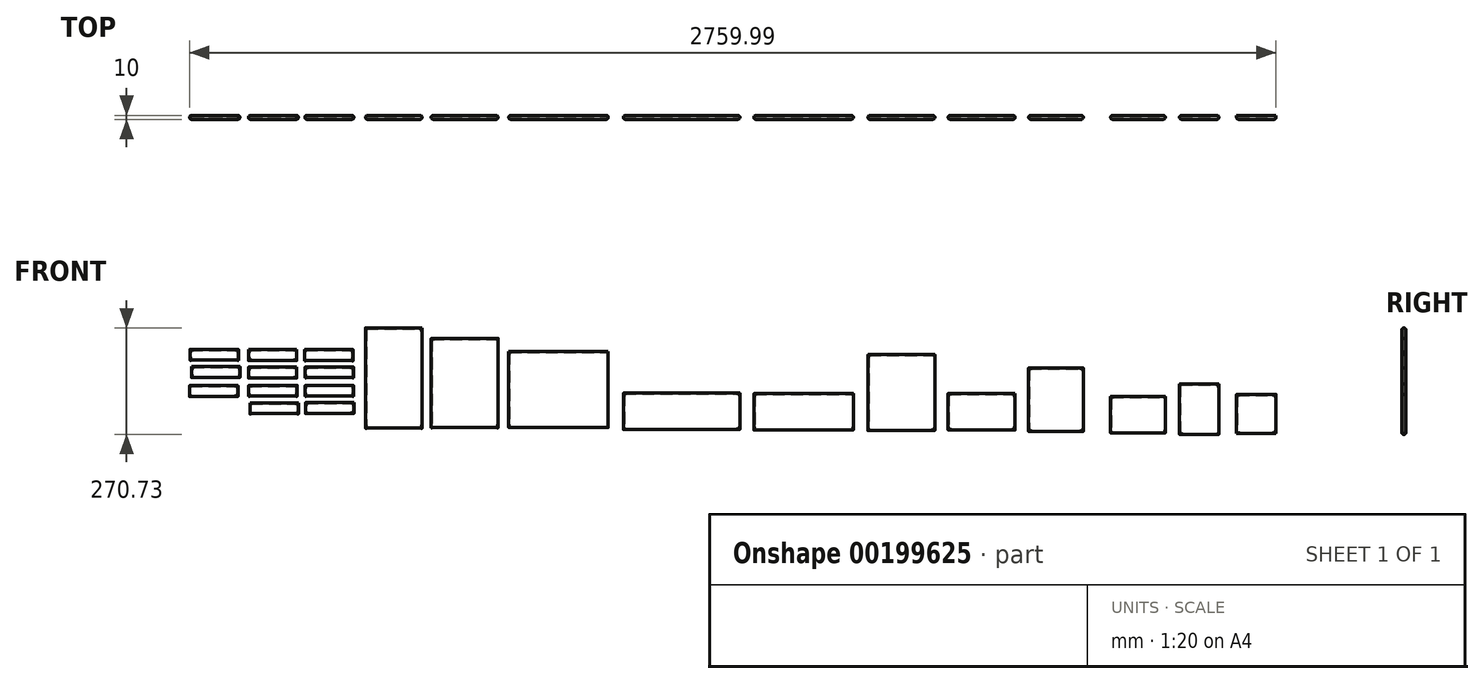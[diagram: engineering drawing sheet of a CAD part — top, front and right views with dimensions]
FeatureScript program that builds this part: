
annotation { "Feature Type Name" : "Feature", "Feature Type Description" : "" }
export const myFeature = defineFeature(function(context is Context, id is Id, definition is map)
    precondition{}
    {
        {
            var Q0;
            Q0=qCreatedBy(makeId("Front.planeOp"),FACE);
            var sketch = newSketch(context, id + "F0", { "sketchPlane" : qUnion([Q0])});
            skLineSegment(sketch, "E0.bottom", {"start": v(-185.42, 51.02) * mm, "end": v(-62.42, 51.02) * mm});
            skLineSegment(sketch, "E0.top", {"start": v(-185.42, 79.02) * mm, "end": v(-62.42, 79.02) * mm});
            skLineSegment(sketch, "E0.left", {"start": v(-185.42, 51.02) * mm, "end": v(-185.42, 79.02) * mm});
            skLineSegment(sketch, "E0.right", {"start": v(-62.42, 51.02) * mm, "end": v(-62.42, 79.02) * mm});
            skLineSegment(sketch, "E1.bottom", {"start": v(-184.61, -39.22) * mm, "end": v(-61.61, -39.22) * mm});
            skLineSegment(sketch, "E1.top", {"start": v(-184.61, -11.22) * mm, "end": v(-61.61, -11.22) * mm});
            skLineSegment(sketch, "E1.left", {"start": v(-184.61, -39.22) * mm, "end": v(-184.61, -11.22) * mm});
            skLineSegment(sketch, "E1.right", {"start": v(-61.61, -39.22) * mm, "end": v(-61.61, -11.22) * mm});
            skLineSegment(sketch, "E2.bottom", {"start": v(-183.78, -83.5) * mm, "end": v(-60.78, -83.5) * mm});
            skLineSegment(sketch, "E2.top", {"start": v(-183.78, -55.5) * mm, "end": v(-60.78, -55.5) * mm});
            skLineSegment(sketch, "E2.left", {"start": v(-183.78, -83.5) * mm, "end": v(-183.78, -55.5) * mm});
            skLineSegment(sketch, "E2.right", {"start": v(-60.78, -83.5) * mm, "end": v(-60.78, -55.5) * mm});
            skLineSegment(sketch, "E3.bottom", {"start": v(-328.72, 51.62) * mm, "end": v(-205.72, 51.62) * mm});
            skLineSegment(sketch, "E3.top", {"start": v(-328.72, 79.62) * mm, "end": v(-205.72, 79.62) * mm});
            skLineSegment(sketch, "E3.left", {"start": v(-328.72, 51.62) * mm, "end": v(-328.72, 79.62) * mm});
            skLineSegment(sketch, "E3.right", {"start": v(-205.72, 51.62) * mm, "end": v(-205.72, 79.62) * mm});
            skLineSegment(sketch, "E4.bottom", {"start": v(-184.79, 7.45) * mm, "end": v(-61.79, 7.45) * mm});
            skLineSegment(sketch, "E4.top", {"start": v(-184.79, 35.45) * mm, "end": v(-61.79, 35.45) * mm});
            skLineSegment(sketch, "E4.left", {"start": v(-184.79, 7.45) * mm, "end": v(-184.79, 35.45) * mm});
            skLineSegment(sketch, "E4.right", {"start": v(-61.79, 7.45) * mm, "end": v(-61.79, 35.45) * mm});
            skLineSegment(sketch, "E5.bottom", {"start": v(-328.7, 6.95) * mm, "end": v(-205.7, 6.95) * mm});
            skLineSegment(sketch, "E5.top", {"start": v(-328.7, 34.95) * mm, "end": v(-205.7, 34.95) * mm});
            skLineSegment(sketch, "E5.left", {"start": v(-328.7, 6.95) * mm, "end": v(-328.7, 34.95) * mm});
            skLineSegment(sketch, "E5.right", {"start": v(-205.7, 6.95) * mm, "end": v(-205.7, 34.95) * mm});
            skLineSegment(sketch, "E6.bottom", {"start": v(-477.03, 51.95) * mm, "end": v(-354.03, 51.95) * mm});
            skLineSegment(sketch, "E6.top", {"start": v(-477.03, 79.95) * mm, "end": v(-354.03, 79.95) * mm});
            skLineSegment(sketch, "E6.left", {"start": v(-477.03, 51.95) * mm, "end": v(-477.03, 79.95) * mm});
            skLineSegment(sketch, "E6.right", {"start": v(-354.03, 51.95) * mm, "end": v(-354.03, 79.95) * mm});
            skLineSegment(sketch, "E7.bottom", {"start": v(-473.24, 7.86) * mm, "end": v(-350.24, 7.86) * mm});
            skLineSegment(sketch, "E7.top", {"start": v(-473.24, 35.86) * mm, "end": v(-350.24, 35.86) * mm});
            skLineSegment(sketch, "E7.left", {"start": v(-473.24, 7.86) * mm, "end": v(-473.24, 35.86) * mm});
            skLineSegment(sketch, "E7.right", {"start": v(-350.24, 7.86) * mm, "end": v(-350.24, 35.86) * mm});
            skLineSegment(sketch, "E8.bottom", {"start": v(-478.2, -39.92) * mm, "end": v(-355.2, -39.92) * mm});
            skLineSegment(sketch, "E8.top", {"start": v(-478.2, -11.92) * mm, "end": v(-355.2, -11.92) * mm});
            skLineSegment(sketch, "E8.left", {"start": v(-478.2, -39.92) * mm, "end": v(-478.2, -11.92) * mm});
            skLineSegment(sketch, "E8.right", {"start": v(-355.2, -39.92) * mm, "end": v(-355.2, -11.92) * mm});
            skLineSegment(sketch, "E9.bottom", {"start": v(-324.63, -84.24) * mm, "end": v(-201.63, -84.24) * mm});
            skLineSegment(sketch, "E9.top", {"start": v(-324.63, -56.24) * mm, "end": v(-201.63, -56.24) * mm});
            skLineSegment(sketch, "E9.left", {"start": v(-324.63, -84.24) * mm, "end": v(-324.63, -56.24) * mm});
            skLineSegment(sketch, "E9.right", {"start": v(-201.63, -84.24) * mm, "end": v(-201.63, -56.24) * mm});
            skLineSegment(sketch, "E10.bottom", {"start": v(-327.71, -39.33) * mm, "end": v(-204.71, -39.33) * mm});
            skLineSegment(sketch, "E10.top", {"start": v(-327.71, -11.33) * mm, "end": v(-204.71, -11.33) * mm});
            skLineSegment(sketch, "E10.left", {"start": v(-327.71, -39.33) * mm, "end": v(-327.71, -11.33) * mm});
            skLineSegment(sketch, "E10.right", {"start": v(-204.71, -39.33) * mm, "end": v(-204.71, -11.33) * mm});
            skSolve(sketch);
        }
        {
            var Q0;
            Q0=qSketchRegion(id+"F0",true);
            extrude(context, id + "F1", {"entities" : qUnion([Q0]), "depth" : 10 * mm});
        }
        {
            var Q0;
            Q0=makeQuery(id+"F1.opExtrude","SWEPT_FACE",FACE,{"disambiguationData":[OSD([sQuery(id+"F0.wireOp",EDGE,"E0.bottom")])]});
            var Q1;
            Q1=makeQuery(id+"F1.opExtrude","SWEPT_FACE",FACE,{"disambiguationData":[OSD([sQuery(id+"F0.wireOp",EDGE,"E4.bottom")])]});
            var Q2;
            Q2=makeQuery(id+"F1.opExtrude","SWEPT_FACE",FACE,{"disambiguationData":[OSD([sQuery(id+"F0.wireOp",EDGE,"E7.bottom")])]});
            var Q3;
            Q3=makeQuery(id+"F1.opExtrude","SWEPT_FACE",FACE,{"disambiguationData":[OSD([sQuery(id+"F0.wireOp",EDGE,"E3.bottom")])]});
            var Q4;
            Q4=makeQuery(id+"F1.opExtrude","SWEPT_FACE",FACE,{"disambiguationData":[OSD([sQuery(id+"F0.wireOp",EDGE,"E6.bottom")])]});
            var Q5;
            Q5=makeQuery(id+"F1.opExtrude","SWEPT_FACE",FACE,{"disambiguationData":[OSD([sQuery(id+"F0.wireOp",EDGE,"E8.bottom")])]});
            var Q6;
            Q6=makeQuery(id+"F1.opExtrude","SWEPT_FACE",FACE,{"disambiguationData":[OSD([sQuery(id+"F0.wireOp",EDGE,"E9.bottom")])]});
            var Q7;
            Q7=makeQuery(id+"F1.opExtrude","SWEPT_FACE",FACE,{"disambiguationData":[OSD([sQuery(id+"F0.wireOp",EDGE,"E10.bottom")])]});
            var Q8;
            Q8=makeQuery(id+"F1.opExtrude","SWEPT_FACE",FACE,{"disambiguationData":[OSD([sQuery(id+"F0.wireOp",EDGE,"E5.bottom")])]});
            var Q9;
            Q9=makeQuery(id+"F1.opExtrude","SWEPT_FACE",FACE,{"disambiguationData":[OSD([sQuery(id+"F0.wireOp",EDGE,"E2.bottom")])]});
            var Q10;
            Q10=makeQuery(id+"F1.opExtrude","SWEPT_FACE",FACE,{"disambiguationData":[OSD([sQuery(id+"F0.wireOp",EDGE,"E1.bottom")])]});
            shell(context, id + "F2", {"entities" : qUnion([Q0, Q1, Q2, Q3, Q4, Q5, Q6, Q7, Q8, Q9, Q10]), "thickness" : 2.5 * mm});
        }
        {
            var Q0;
            Q0=qCreatedBy(makeId("Front.planeOp"),FACE);
            var sketch = newSketch(context, id + "F3", { "sketchPlane" : qUnion([Q0])});
            skLineSegment(sketch, "E11.bottom", {"start": v(-31.23, 134.3) * mm, "end": v(112.77, 134.3) * mm});
            skLineSegment(sketch, "E11.top", {"start": v(-31.23, -120.7) * mm, "end": v(112.77, -120.7) * mm});
            skLineSegment(sketch, "E11.left", {"start": v(-31.23, 134.3) * mm, "end": v(-31.23, -120.7) * mm});
            skLineSegment(sketch, "E11.right", {"start": v(112.77, 134.3) * mm, "end": v(112.77, -120.7) * mm});
            skLineSegment(sketch, "E12.bottom", {"start": v(135.53, 107.6) * mm, "end": v(305.53, 107.6) * mm});
            skLineSegment(sketch, "E12.top", {"start": v(135.53, -119.4) * mm, "end": v(305.53, -119.4) * mm});
            skLineSegment(sketch, "E12.left", {"start": v(135.53, 107.6) * mm, "end": v(135.53, -119.4) * mm});
            skLineSegment(sketch, "E12.right", {"start": v(305.53, 107.6) * mm, "end": v(305.53, -119.4) * mm});
            skLineSegment(sketch, "E13.bottom", {"start": v(332.44, 73.9) * mm, "end": v(585.44, 73.9) * mm});
            skLineSegment(sketch, "E13.top", {"start": v(332.44, -119.1) * mm, "end": v(585.44, -119.1) * mm});
            skLineSegment(sketch, "E13.left", {"start": v(332.44, 73.9) * mm, "end": v(332.44, -119.1) * mm});
            skLineSegment(sketch, "E13.right", {"start": v(585.44, 73.9) * mm, "end": v(585.44, -119.1) * mm});
            skLineSegment(sketch, "E14.bottom", {"start": v(623.81, -30.97) * mm, "end": v(919.81, -30.97) * mm});
            skLineSegment(sketch, "E14.top", {"start": v(623.81, -123.97) * mm, "end": v(919.81, -123.97) * mm});
            skLineSegment(sketch, "E14.left", {"start": v(623.81, -30.97) * mm, "end": v(623.81, -123.97) * mm});
            skLineSegment(sketch, "E14.right", {"start": v(919.81, -30.97) * mm, "end": v(919.81, -123.97) * mm});
            skLineSegment(sketch, "E15.bottom", {"start": v(955.2, -32.5) * mm, "end": v(1208.2, -32.5) * mm});
            skLineSegment(sketch, "E15.top", {"start": v(955.2, -125.5) * mm, "end": v(1208.2, -125.5) * mm});
            skLineSegment(sketch, "E15.left", {"start": v(955.2, -32.5) * mm, "end": v(955.2, -125.5) * mm});
            skLineSegment(sketch, "E15.right", {"start": v(1208.2, -32.5) * mm, "end": v(1208.2, -125.5) * mm});
            skLineSegment(sketch, "E16.bottom", {"start": v(1245.22, 66.68) * mm, "end": v(1415.22, 66.68) * mm});
            skLineSegment(sketch, "E16.top", {"start": v(1245.22, -126.32) * mm, "end": v(1415.22, -126.32) * mm});
            skLineSegment(sketch, "E16.left", {"start": v(1245.22, 66.68) * mm, "end": v(1245.22, -126.32) * mm});
            skLineSegment(sketch, "E16.right", {"start": v(1415.22, 66.68) * mm, "end": v(1415.22, -126.32) * mm});
            skLineSegment(sketch, "E17.bottom", {"start": v(1448.93, -32.02) * mm, "end": v(1618.93, -32.02) * mm});
            skLineSegment(sketch, "E17.top", {"start": v(1448.93, -125.02) * mm, "end": v(1618.93, -125.02) * mm});
            skLineSegment(sketch, "E17.left", {"start": v(1448.93, -32.02) * mm, "end": v(1448.93, -125.02) * mm});
            skLineSegment(sketch, "E17.right", {"start": v(1618.93, -32.02) * mm, "end": v(1618.93, -125.02) * mm});
            skLineSegment(sketch, "E18.bottom", {"start": v(1653.54, 32.98) * mm, "end": v(1792.54, 32.98) * mm});
            skLineSegment(sketch, "E18.top", {"start": v(1653.54, -129.02) * mm, "end": v(1792.54, -129.02) * mm});
            skLineSegment(sketch, "E18.left", {"start": v(1653.54, 32.98) * mm, "end": v(1653.54, -129.02) * mm});
            skLineSegment(sketch, "E18.right", {"start": v(1792.54, 32.98) * mm, "end": v(1792.54, -129.02) * mm});
            skLineSegment(sketch, "E19.bottom", {"start": v(1861.67, -40.12) * mm, "end": v(2000.67, -40.12) * mm});
            skLineSegment(sketch, "E19.top", {"start": v(1861.67, -133.12) * mm, "end": v(2000.67, -133.12) * mm});
            skLineSegment(sketch, "E19.left", {"start": v(1861.67, -40.12) * mm, "end": v(1861.67, -133.12) * mm});
            skLineSegment(sketch, "E19.right", {"start": v(2000.67, -40.12) * mm, "end": v(2000.67, -133.12) * mm});
            skLineSegment(sketch, "E20.bottom", {"start": v(2036.78, -8.43) * mm, "end": v(2136.78, -8.43) * mm});
            skLineSegment(sketch, "E20.top", {"start": v(2036.78, -136.43) * mm, "end": v(2136.78, -136.43) * mm});
            skLineSegment(sketch, "E20.left", {"start": v(2036.78, -8.43) * mm, "end": v(2036.78, -136.43) * mm});
            skLineSegment(sketch, "E20.right", {"start": v(2136.78, -8.43) * mm, "end": v(2136.78, -136.43) * mm});
            skLineSegment(sketch, "E21.bottom", {"start": v(2181.78, -34.27) * mm, "end": v(2281.78, -34.27) * mm});
            skLineSegment(sketch, "E21.top", {"start": v(2181.78, -134.27) * mm, "end": v(2281.78, -134.27) * mm});
            skLineSegment(sketch, "E21.left", {"start": v(2181.78, -34.27) * mm, "end": v(2181.78, -134.27) * mm});
            skLineSegment(sketch, "E21.right", {"start": v(2281.78, -34.27) * mm, "end": v(2281.78, -134.27) * mm});
            skSolve(sketch);
        }
        {
            var Q0;
            Q0=qSketchRegion(id+"F3",true);
            extrude(context, id + "F4", {"entities" : qUnion([Q0]), "depth" : 10 * mm});
        }
        {
            var Q0;
            Q0=makeQuery(id+"F4.opExtrude","SWEPT_FACE",FACE,{"disambiguationData":[OSD([sQuery(id+"F3.wireOp",EDGE,"E11.top")])]});
            var Q1;
            Q1=makeQuery(id+"F4.opExtrude","SWEPT_FACE",FACE,{"disambiguationData":[OSD([sQuery(id+"F3.wireOp",EDGE,"E12.top")])]});
            var Q2;
            Q2=makeQuery(id+"F4.opExtrude","SWEPT_FACE",FACE,{"disambiguationData":[OSD([sQuery(id+"F3.wireOp",EDGE,"E13.top")])]});
            var Q3;
            Q3=makeQuery(id+"F4.opExtrude","SWEPT_FACE",FACE,{"disambiguationData":[OSD([sQuery(id+"F3.wireOp",EDGE,"E14.top")])]});
            var Q4;
            Q4=makeQuery(id+"F4.opExtrude","SWEPT_FACE",FACE,{"disambiguationData":[OSD([sQuery(id+"F3.wireOp",EDGE,"E15.top")])]});
            var Q5;
            Q5=makeQuery(id+"F4.opExtrude","SWEPT_FACE",FACE,{"disambiguationData":[OSD([sQuery(id+"F3.wireOp",EDGE,"E16.top")])]});
            var Q6;
            Q6=makeQuery(id+"F4.opExtrude","SWEPT_FACE",FACE,{"disambiguationData":[OSD([sQuery(id+"F3.wireOp",EDGE,"E17.top")])]});
            var Q7;
            Q7=makeQuery(id+"F4.opExtrude","SWEPT_FACE",FACE,{"disambiguationData":[OSD([sQuery(id+"F3.wireOp",EDGE,"E18.top")])]});
            var Q8;
            Q8=makeQuery(id+"F4.opExtrude","SWEPT_FACE",FACE,{"disambiguationData":[OSD([sQuery(id+"F3.wireOp",EDGE,"E19.top")])]});
            var Q9;
            Q9=makeQuery(id+"F4.opExtrude","SWEPT_FACE",FACE,{"disambiguationData":[OSD([sQuery(id+"F3.wireOp",EDGE,"E20.top")])]});
            var Q10;
            Q10=makeQuery(id+"F4.opExtrude","SWEPT_FACE",FACE,{"disambiguationData":[OSD([sQuery(id+"F3.wireOp",EDGE,"E21.top")])]});
            shell(context, id + "F5", {"entities" : qUnion([Q0, Q1, Q2, Q3, Q4, Q5, Q6, Q7, Q8, Q9, Q10]), "thickness" : 2.5 * mm});
        }
        {
            var Q0;
            Q0=makeQuery(id+"F4.opExtrude","CAP_FACE",FACE,{"disambiguationData":[OSD([sQuery(id+"F3.wireOp",EDGE,"E11.bottom"),sQuery(id+"F3.wireOp",EDGE,"E11.top"),sQuery(id+"F3.wireOp",EDGE,"E11.left"),sQuery(id+"F3.wireOp",EDGE,"E11.right")])],"isStart":false});
            var Q1;
            Q1=makeQuery(id+"F4.opExtrude","CAP_FACE",FACE,{"disambiguationData":[OSD([sQuery(id+"F3.wireOp",EDGE,"E12.bottom"),sQuery(id+"F3.wireOp",EDGE,"E12.top"),sQuery(id+"F3.wireOp",EDGE,"E12.left"),sQuery(id+"F3.wireOp",EDGE,"E12.right")])],"isStart":false});
            var Q2;
            Q2=makeQuery(id+"F4.opExtrude","CAP_FACE",FACE,{"disambiguationData":[OSD([sQuery(id+"F3.wireOp",EDGE,"E13.bottom"),sQuery(id+"F3.wireOp",EDGE,"E13.top"),sQuery(id+"F3.wireOp",EDGE,"E13.left"),sQuery(id+"F3.wireOp",EDGE,"E13.right")])],"isStart":false});
            var Q3;
            Q3=makeQuery(id+"F4.opExtrude","CAP_FACE",FACE,{"disambiguationData":[OSD([sQuery(id+"F3.wireOp",EDGE,"E14.bottom"),sQuery(id+"F3.wireOp",EDGE,"E14.top"),sQuery(id+"F3.wireOp",EDGE,"E14.left"),sQuery(id+"F3.wireOp",EDGE,"E14.right")])],"isStart":false});
            var Q4;
            Q4=makeQuery(id+"F4.opExtrude","CAP_FACE",FACE,{"disambiguationData":[OSD([sQuery(id+"F3.wireOp",EDGE,"E15.bottom"),sQuery(id+"F3.wireOp",EDGE,"E15.top"),sQuery(id+"F3.wireOp",EDGE,"E15.left"),sQuery(id+"F3.wireOp",EDGE,"E15.right")])],"isStart":false});
            var Q5;
            Q5=makeQuery(id+"F4.opExtrude","CAP_FACE",FACE,{"disambiguationData":[OSD([sQuery(id+"F3.wireOp",EDGE,"E16.bottom"),sQuery(id+"F3.wireOp",EDGE,"E16.top"),sQuery(id+"F3.wireOp",EDGE,"E16.left"),sQuery(id+"F3.wireOp",EDGE,"E16.right")])],"isStart":false});
            var Q6;
            Q6=makeQuery(id+"F4.opExtrude","CAP_FACE",FACE,{"disambiguationData":[OSD([sQuery(id+"F3.wireOp",EDGE,"E17.bottom"),sQuery(id+"F3.wireOp",EDGE,"E17.top"),sQuery(id+"F3.wireOp",EDGE,"E17.left"),sQuery(id+"F3.wireOp",EDGE,"E17.right")])],"isStart":false});
            var Q7;
            Q7=makeQuery(id+"F4.opExtrude","CAP_FACE",FACE,{"disambiguationData":[OSD([sQuery(id+"F3.wireOp",EDGE,"E18.bottom"),sQuery(id+"F3.wireOp",EDGE,"E18.top"),sQuery(id+"F3.wireOp",EDGE,"E18.left"),sQuery(id+"F3.wireOp",EDGE,"E18.right")])],"isStart":false});
            var Q8;
            Q8=makeQuery(id+"F4.opExtrude","CAP_FACE",FACE,{"disambiguationData":[OSD([sQuery(id+"F3.wireOp",EDGE,"E19.bottom"),sQuery(id+"F3.wireOp",EDGE,"E19.top"),sQuery(id+"F3.wireOp",EDGE,"E19.left"),sQuery(id+"F3.wireOp",EDGE,"E19.right")])],"isStart":false});
            var Q9;
            Q9=makeQuery(id+"F4.opExtrude","CAP_FACE",FACE,{"disambiguationData":[OSD([sQuery(id+"F3.wireOp",EDGE,"E20.bottom"),sQuery(id+"F3.wireOp",EDGE,"E20.top"),sQuery(id+"F3.wireOp",EDGE,"E20.left"),sQuery(id+"F3.wireOp",EDGE,"E20.right")])],"isStart":false});
            var Q10;
            Q10=makeQuery(id+"F4.opExtrude","CAP_FACE",FACE,{"disambiguationData":[OSD([sQuery(id+"F3.wireOp",EDGE,"E21.bottom"),sQuery(id+"F3.wireOp",EDGE,"E21.top"),sQuery(id+"F3.wireOp",EDGE,"E21.left"),sQuery(id+"F3.wireOp",EDGE,"E21.right")])],"isStart":false});
            var Q11;
            Q11=makeQuery(id+"F4.opExtrude","CAP_FACE",FACE,{"disambiguationData":[OSD([sQuery(id+"F3.wireOp",EDGE,"E20.bottom"),sQuery(id+"F3.wireOp",EDGE,"E20.top"),sQuery(id+"F3.wireOp",EDGE,"E20.left"),sQuery(id+"F3.wireOp",EDGE,"E20.right")])],"isStart":true});
            var Q12;
            Q12=makeQuery(id+"F4.opExtrude","CAP_FACE",FACE,{"disambiguationData":[OSD([sQuery(id+"F3.wireOp",EDGE,"E19.bottom"),sQuery(id+"F3.wireOp",EDGE,"E19.top"),sQuery(id+"F3.wireOp",EDGE,"E19.left"),sQuery(id+"F3.wireOp",EDGE,"E19.right")])],"isStart":true});
            var Q13;
            Q13=makeQuery(id+"F4.opExtrude","CAP_FACE",FACE,{"disambiguationData":[OSD([sQuery(id+"F3.wireOp",EDGE,"E18.bottom"),sQuery(id+"F3.wireOp",EDGE,"E18.top"),sQuery(id+"F3.wireOp",EDGE,"E18.left"),sQuery(id+"F3.wireOp",EDGE,"E18.right")])],"isStart":true});
            var Q14;
            Q14=makeQuery(id+"F4.opExtrude","CAP_FACE",FACE,{"disambiguationData":[OSD([sQuery(id+"F3.wireOp",EDGE,"E17.bottom"),sQuery(id+"F3.wireOp",EDGE,"E17.top"),sQuery(id+"F3.wireOp",EDGE,"E17.left"),sQuery(id+"F3.wireOp",EDGE,"E17.right")])],"isStart":true});
            var Q15;
            Q15=makeQuery(id+"F4.opExtrude","CAP_FACE",FACE,{"disambiguationData":[OSD([sQuery(id+"F3.wireOp",EDGE,"E16.bottom"),sQuery(id+"F3.wireOp",EDGE,"E16.top"),sQuery(id+"F3.wireOp",EDGE,"E16.left"),sQuery(id+"F3.wireOp",EDGE,"E16.right")])],"isStart":true});
            var Q16;
            Q16=makeQuery(id+"F4.opExtrude","CAP_FACE",FACE,{"disambiguationData":[OSD([sQuery(id+"F3.wireOp",EDGE,"E15.bottom"),sQuery(id+"F3.wireOp",EDGE,"E15.top"),sQuery(id+"F3.wireOp",EDGE,"E15.left"),sQuery(id+"F3.wireOp",EDGE,"E15.right")])],"isStart":true});
            var Q17;
            Q17=makeQuery(id+"F4.opExtrude","CAP_FACE",FACE,{"disambiguationData":[OSD([sQuery(id+"F3.wireOp",EDGE,"E14.bottom"),sQuery(id+"F3.wireOp",EDGE,"E14.top"),sQuery(id+"F3.wireOp",EDGE,"E14.left"),sQuery(id+"F3.wireOp",EDGE,"E14.right")])],"isStart":true});
            var Q18;
            Q18=makeQuery(id+"F4.opExtrude","CAP_FACE",FACE,{"disambiguationData":[OSD([sQuery(id+"F3.wireOp",EDGE,"E13.bottom"),sQuery(id+"F3.wireOp",EDGE,"E13.top"),sQuery(id+"F3.wireOp",EDGE,"E13.left"),sQuery(id+"F3.wireOp",EDGE,"E13.right")])],"isStart":true});
            var Q19;
            Q19=makeQuery(id+"F4.opExtrude","CAP_FACE",FACE,{"disambiguationData":[OSD([sQuery(id+"F3.wireOp",EDGE,"E12.bottom"),sQuery(id+"F3.wireOp",EDGE,"E12.top"),sQuery(id+"F3.wireOp",EDGE,"E12.left"),sQuery(id+"F3.wireOp",EDGE,"E12.right")])],"isStart":true});
            var Q20;
            Q20=makeQuery(id+"F4.opExtrude","CAP_FACE",FACE,{"disambiguationData":[OSD([sQuery(id+"F3.wireOp",EDGE,"E11.bottom"),sQuery(id+"F3.wireOp",EDGE,"E11.top"),sQuery(id+"F3.wireOp",EDGE,"E11.left"),sQuery(id+"F3.wireOp",EDGE,"E11.right")])],"isStart":true});
            var Q21;
            Q21=makeQuery(id+"F1.opExtrude","CAP_FACE",FACE,{"disambiguationData":[OSD([sQuery(id+"F0.wireOp",EDGE,"E0.bottom"),sQuery(id+"F0.wireOp",EDGE,"E0.top"),sQuery(id+"F0.wireOp",EDGE,"E0.left"),sQuery(id+"F0.wireOp",EDGE,"E0.right")])],"isStart":false});
            var Q22;
            Q22=makeQuery(id+"F1.opExtrude","CAP_FACE",FACE,{"disambiguationData":[OSD([sQuery(id+"F0.wireOp",EDGE,"E0.bottom"),sQuery(id+"F0.wireOp",EDGE,"E0.top"),sQuery(id+"F0.wireOp",EDGE,"E0.left"),sQuery(id+"F0.wireOp",EDGE,"E0.right")])],"isStart":true});
            var Q23;
            Q23=makeQuery(id+"F1.opExtrude","CAP_FACE",FACE,{"disambiguationData":[OSD([sQuery(id+"F0.wireOp",EDGE,"E4.bottom"),sQuery(id+"F0.wireOp",EDGE,"E4.top"),sQuery(id+"F0.wireOp",EDGE,"E4.left"),sQuery(id+"F0.wireOp",EDGE,"E4.right")])],"isStart":false});
            var Q24;
            Q24=makeQuery(id+"F1.opExtrude","CAP_FACE",FACE,{"disambiguationData":[OSD([sQuery(id+"F0.wireOp",EDGE,"E3.bottom"),sQuery(id+"F0.wireOp",EDGE,"E3.top"),sQuery(id+"F0.wireOp",EDGE,"E3.left"),sQuery(id+"F0.wireOp",EDGE,"E3.right")])],"isStart":false});
            var Q25;
            Q25=makeQuery(id+"F1.opExtrude","CAP_FACE",FACE,{"disambiguationData":[OSD([sQuery(id+"F0.wireOp",EDGE,"E2.bottom"),sQuery(id+"F0.wireOp",EDGE,"E2.top"),sQuery(id+"F0.wireOp",EDGE,"E2.left"),sQuery(id+"F0.wireOp",EDGE,"E2.right")])],"isStart":false});
            var Q26;
            Q26=makeQuery(id+"F1.opExtrude","CAP_FACE",FACE,{"disambiguationData":[OSD([sQuery(id+"F0.wireOp",EDGE,"E1.bottom"),sQuery(id+"F0.wireOp",EDGE,"E1.top"),sQuery(id+"F0.wireOp",EDGE,"E1.left"),sQuery(id+"F0.wireOp",EDGE,"E1.right")])],"isStart":false});
            var Q27;
            Q27=makeQuery(id+"F1.opExtrude","CAP_FACE",FACE,{"disambiguationData":[OSD([sQuery(id+"F0.wireOp",EDGE,"E5.bottom"),sQuery(id+"F0.wireOp",EDGE,"E5.top"),sQuery(id+"F0.wireOp",EDGE,"E5.left"),sQuery(id+"F0.wireOp",EDGE,"E5.right")])],"isStart":false});
            var Q28;
            Q28=makeQuery(id+"F1.opExtrude","CAP_FACE",FACE,{"disambiguationData":[OSD([sQuery(id+"F0.wireOp",EDGE,"E7.bottom"),sQuery(id+"F0.wireOp",EDGE,"E7.top"),sQuery(id+"F0.wireOp",EDGE,"E7.left"),sQuery(id+"F0.wireOp",EDGE,"E7.right")])],"isStart":false});
            var Q29;
            Q29=makeQuery(id+"F1.opExtrude","CAP_FACE",FACE,{"disambiguationData":[OSD([sQuery(id+"F0.wireOp",EDGE,"E6.bottom"),sQuery(id+"F0.wireOp",EDGE,"E6.top"),sQuery(id+"F0.wireOp",EDGE,"E6.left"),sQuery(id+"F0.wireOp",EDGE,"E6.right")])],"isStart":false});
            var Q30;
            Q30=makeQuery(id+"F1.opExtrude","CAP_FACE",FACE,{"disambiguationData":[OSD([sQuery(id+"F0.wireOp",EDGE,"E8.bottom"),sQuery(id+"F0.wireOp",EDGE,"E8.top"),sQuery(id+"F0.wireOp",EDGE,"E8.left"),sQuery(id+"F0.wireOp",EDGE,"E8.right")])],"isStart":false});
            var Q31;
            Q31=makeQuery(id+"F1.opExtrude","CAP_FACE",FACE,{"disambiguationData":[OSD([sQuery(id+"F0.wireOp",EDGE,"E9.bottom"),sQuery(id+"F0.wireOp",EDGE,"E9.top"),sQuery(id+"F0.wireOp",EDGE,"E9.left"),sQuery(id+"F0.wireOp",EDGE,"E9.right")])],"isStart":false});
            var Q32;
            Q32=makeQuery(id+"F1.opExtrude","CAP_FACE",FACE,{"disambiguationData":[OSD([sQuery(id+"F0.wireOp",EDGE,"E10.bottom"),sQuery(id+"F0.wireOp",EDGE,"E10.top"),sQuery(id+"F0.wireOp",EDGE,"E10.left"),sQuery(id+"F0.wireOp",EDGE,"E10.right")])],"isStart":false});
            var Q33;
            Q33=makeQuery(id+"F1.opExtrude","CAP_FACE",FACE,{"disambiguationData":[OSD([sQuery(id+"F0.wireOp",EDGE,"E10.bottom"),sQuery(id+"F0.wireOp",EDGE,"E10.top"),sQuery(id+"F0.wireOp",EDGE,"E10.left"),sQuery(id+"F0.wireOp",EDGE,"E10.right")])],"isStart":true});
            var Q34;
            Q34=makeQuery(id+"F1.opExtrude","CAP_FACE",FACE,{"disambiguationData":[OSD([sQuery(id+"F0.wireOp",EDGE,"E1.bottom"),sQuery(id+"F0.wireOp",EDGE,"E1.top"),sQuery(id+"F0.wireOp",EDGE,"E1.left"),sQuery(id+"F0.wireOp",EDGE,"E1.right")])],"isStart":true});
            var Q35;
            Q35=makeQuery(id+"F1.opExtrude","CAP_FACE",FACE,{"disambiguationData":[OSD([sQuery(id+"F0.wireOp",EDGE,"E5.bottom"),sQuery(id+"F0.wireOp",EDGE,"E5.top"),sQuery(id+"F0.wireOp",EDGE,"E5.left"),sQuery(id+"F0.wireOp",EDGE,"E5.right")])],"isStart":true});
            var Q36;
            Q36=makeQuery(id+"F1.opExtrude","CAP_FACE",FACE,{"disambiguationData":[OSD([sQuery(id+"F0.wireOp",EDGE,"E9.bottom"),sQuery(id+"F0.wireOp",EDGE,"E9.top"),sQuery(id+"F0.wireOp",EDGE,"E9.left"),sQuery(id+"F0.wireOp",EDGE,"E9.right")])],"isStart":true});
            var Q37;
            Q37=makeQuery(id+"F1.opExtrude","CAP_FACE",FACE,{"disambiguationData":[OSD([sQuery(id+"F0.wireOp",EDGE,"E8.bottom"),sQuery(id+"F0.wireOp",EDGE,"E8.top"),sQuery(id+"F0.wireOp",EDGE,"E8.left"),sQuery(id+"F0.wireOp",EDGE,"E8.right")])],"isStart":true});
            var Q38;
            Q38=makeQuery(id+"F1.opExtrude","CAP_FACE",FACE,{"disambiguationData":[OSD([sQuery(id+"F0.wireOp",EDGE,"E2.bottom"),sQuery(id+"F0.wireOp",EDGE,"E2.top"),sQuery(id+"F0.wireOp",EDGE,"E2.left"),sQuery(id+"F0.wireOp",EDGE,"E2.right")])],"isStart":true});
            var Q39;
            Q39=makeQuery(id+"F1.opExtrude","CAP_FACE",FACE,{"disambiguationData":[OSD([sQuery(id+"F0.wireOp",EDGE,"E3.bottom"),sQuery(id+"F0.wireOp",EDGE,"E3.top"),sQuery(id+"F0.wireOp",EDGE,"E3.left"),sQuery(id+"F0.wireOp",EDGE,"E3.right")])],"isStart":true});
            var Q40;
            Q40=makeQuery(id+"F1.opExtrude","CAP_FACE",FACE,{"disambiguationData":[OSD([sQuery(id+"F0.wireOp",EDGE,"E6.bottom"),sQuery(id+"F0.wireOp",EDGE,"E6.top"),sQuery(id+"F0.wireOp",EDGE,"E6.left"),sQuery(id+"F0.wireOp",EDGE,"E6.right")])],"isStart":true});
            var Q41;
            Q41=makeQuery(id+"F1.opExtrude","CAP_FACE",FACE,{"disambiguationData":[OSD([sQuery(id+"F0.wireOp",EDGE,"E4.bottom"),sQuery(id+"F0.wireOp",EDGE,"E4.top"),sQuery(id+"F0.wireOp",EDGE,"E4.left"),sQuery(id+"F0.wireOp",EDGE,"E4.right")])],"isStart":true});
            var Q42;
            Q42=makeQuery(id+"F1.opExtrude","CAP_FACE",FACE,{"disambiguationData":[OSD([sQuery(id+"F0.wireOp",EDGE,"E7.bottom"),sQuery(id+"F0.wireOp",EDGE,"E7.top"),sQuery(id+"F0.wireOp",EDGE,"E7.left"),sQuery(id+"F0.wireOp",EDGE,"E7.right")])],"isStart":true});
            fillet(context, id + "F6", {"entities" : qUnion([Q0, Q1, Q2, Q3, Q4, Q5, Q6, Q7, Q8, Q9, Q10, Q11, Q12, Q13, Q14, Q15, Q16, Q17, Q18, Q19, Q20, Q21, Q22, Q23, Q24, Q25, Q26, Q27, Q28, Q29, Q30, Q31, Q32, Q33, Q34, Q35, Q36, Q37, Q38, Q39, Q40, Q41, Q42]), "radius" : 5 * mm, "tangentPropagation" : true, "allowEdgeOverflow" : false});
        }
    });
